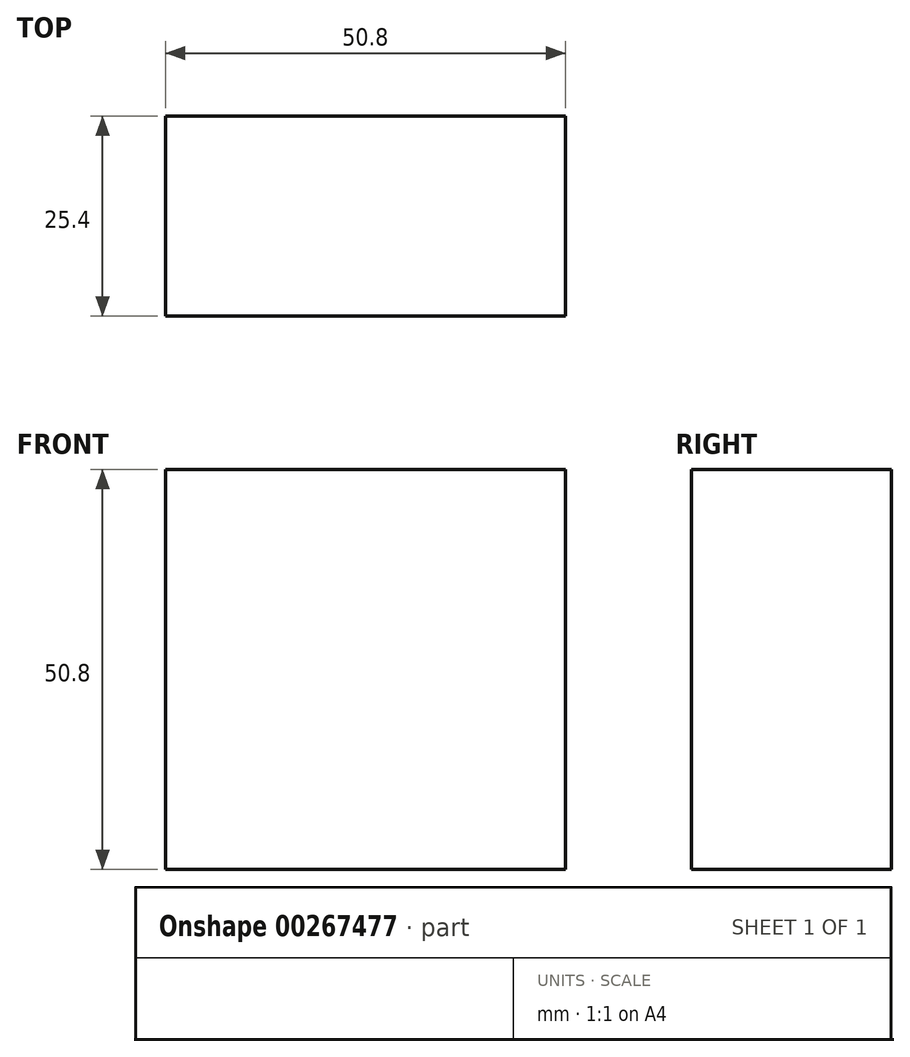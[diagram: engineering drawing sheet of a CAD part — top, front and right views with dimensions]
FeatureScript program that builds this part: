
annotation { "Feature Type Name" : "Feature", "Feature Type Description" : "" }
export const myFeature = defineFeature(function(context is Context, id is Id, definition is map)
    precondition{}
    {
        {
            var Q0;
            Q0=qCreatedBy(makeId("Front.planeOp"),FACE);
            var sketch = newSketch(context, id + "F0", { "sketchPlane" : qUnion([Q0])});
            skLineSegment(sketch, "E0.bottom", {"start": v(25.4, -25.4) * mm, "end": v(-25.4, -25.4) * mm});
            skLineSegment(sketch, "E0.top", {"start": v(25.4, 25.4) * mm, "end": v(-25.4, 25.4) * mm});
            skLineSegment(sketch, "E0.left", {"start": v(25.4, -25.4) * mm, "end": v(25.4, 25.4) * mm});
            skLineSegment(sketch, "E0.right", {"start": v(-25.4, -25.4) * mm, "end": v(-25.4, 25.4) * mm});
            skPoint(sketch, "E0.middle", {"position": v(0, 0) * mm});
            skSolve(sketch);
        }
        {
            var Q0;
            Q0 = qSketchRegion(id + "F0", true);
            extrude(context, id + "F1", {"entities" : qUnion([Q0]), "depth" : 25.4 * mm});
        }
    });
